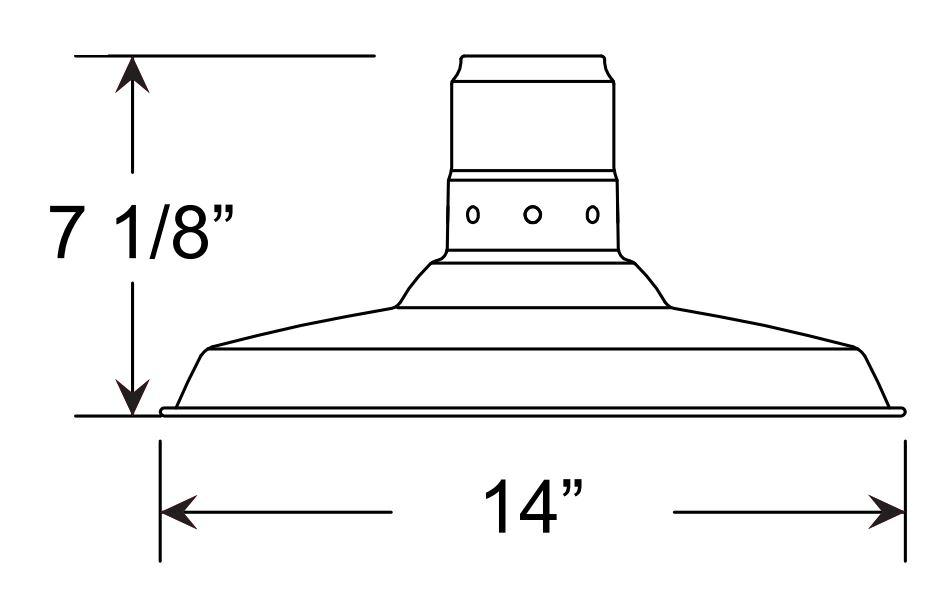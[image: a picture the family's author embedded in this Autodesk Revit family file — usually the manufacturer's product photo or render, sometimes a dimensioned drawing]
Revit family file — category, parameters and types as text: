
# Revit family: Mini Bella Vista_Bell_LED
name_source: partatom
category: Lighting Fixtures
units: mm (PartAtom-declared; Revit-internal decimal feet)

## family parameters
Always vertical = Yes
Cut with Voids When Loaded = No
Light Source = Yes
OmniClass Number = 23.80.70.00
OmniClass Title = Lighting
Part Type = Normal
Room Calculation Point = No
Round Connector Dimension = Use Diameter
Shared = No
Work Plane-Based = No

## types (6) — shared parameters
Body Colour = Spun aluminium
Body Material = body
Bulb = BULB
Color Filter = 16777215
Construction Material = Heavy Duty spun aluminum.
Default Elevation = 0' - 0"
Description = 120-277 Voltage
Dimming = 1%
Dimming Lamp Color Temperature Shift = <None>
Efficiency = 65-125 lumens per watt
GLASS = Glass
Inside body material = INSIDE BODY MATERIAL
Lamp = LED
Life = L70 50,000 hours
Load Classification = Lighting
Manufacturer = ANP Lighting
Power Factor = 1
Tilt Angle = 90.00°
URL = https://www.anplighting.com
Voltage = 277 V
Warranty = 5 year limited warranty

## per-type parameters (varying)
| type | Apparent Load | BVB2001 | BVB2401 | BVB3001 | Bulb_1 | CRI | Fixture Diameter | Fixture Height | INside Platfrom Height | Inside Platform Dia | Inside platform Radius | Led Platfrom | MBVB12 | MBVB14 | MBVB16 | Photometric Web File | Wattage Comments | Weight |
| BVB2001 | 78 VA | Yes | No | No | No | >80 | 1' - 8" | 1' - 2 1/2" | 0' - 3 1/2" | 1' - 6" | 0' - 9" | Yes | No | No | No | BVB2001CPM78W30T540K.ies | 78W | 16.0 lb |
| BVB2401 | 78 VA | No | Yes | No | No | >80 | 2' - 0" | 1' - 4" | 0' - 3" | 1' - 10" | 0' - 11" | Yes | No | No | No | BVB2401CPM78W30T540K.ies | 78W | 19.0 lb |
| BVB3001 | 78 VA | No | No | Yes | No | >80 | 2' - 6" | 1' - 8" | 0' - 3 1/2" | 2' - 3 1/2" | 1' - 2" | Yes | No | No | No | BVB3001CPM78W30T540K.ies | 78W | 25.0 lb |
| MBVB12 | 16 VA | No | No | No | Yes | >90 | 1' - 0" | 0' - 10 1/2" | 0' - 4" | 1' - 8" | 0' - 10" | No | Yes | No | No | MBVB12M016LDDW40K-IES.ies | 16W | 2.15 lb |
| MBVB14 | 24 VA | No | No | No | Yes | >90 | 1' - 2" | 0' - 11 1/2" | 0' - 5" | 1' - 8" | 0' - 10" | No | No | Yes | No | MBVB16E030LDST540K.ies | 24W | 2.3 lb |
| MBVB16 | 24 VA | No | No | No | Yes | >90 | 1' - 4" | 1' - 0 1/2" | 0' - 6" | 1' - 8" | 0' - 10" | No | No | No | Yes | MBVA16E040LDST540K.ies | 24W | 2.6 lb |

note: column(s) folded — value = type name in every type: Model

## geometry (parser evidence)
native form markers: Sweep x53
no freeform markers — native parametric forms only
